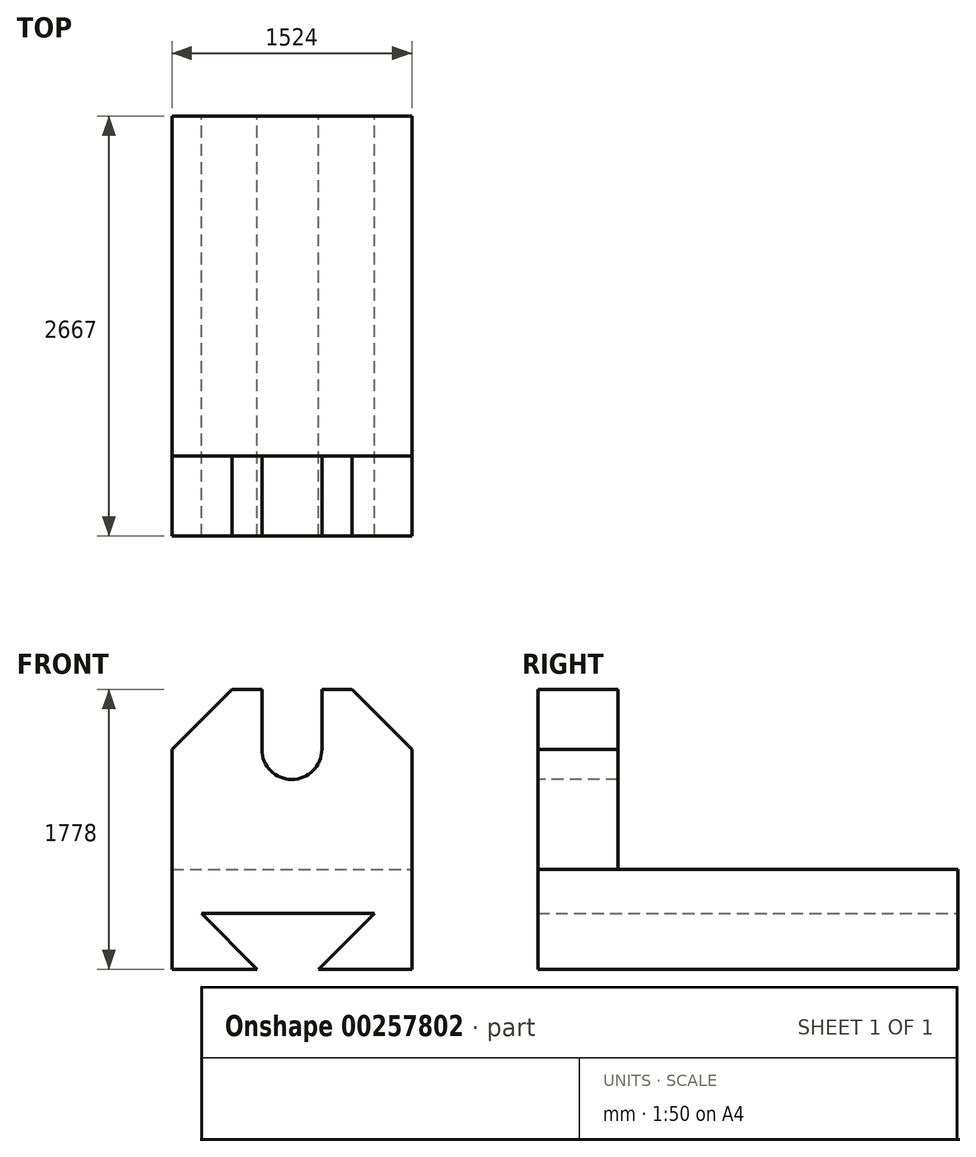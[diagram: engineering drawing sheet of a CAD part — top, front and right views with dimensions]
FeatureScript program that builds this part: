
annotation { "Feature Type Name" : "Feature", "Feature Type Description" : "" }
export const myFeature = defineFeature(function(context is Context, id is Id, definition is map)
    precondition{}
    {
        {
            var Q0;
            Q0=qCreatedBy(makeId("Top.planeOp"),FACE);
            var sketch = newSketch(context, id + "F0", { "sketchPlane" : qUnion([Q0])});
            skLineSegment(sketch, "E0.bottom", {"start": v(-839.6, 1330.28) * mm, "end": v(684.4, 1330.28) * mm});
            skLineSegment(sketch, "E0.top", {"start": v(-839.6, -1336.72) * mm, "end": v(684.4, -1336.72) * mm});
            skLineSegment(sketch, "E0.left", {"start": v(-839.6, 1330.28) * mm, "end": v(-839.6, -1336.72) * mm});
            skLineSegment(sketch, "E0.right", {"start": v(684.4, 1330.28) * mm, "end": v(684.4, -1336.72) * mm});
            skSolve(sketch);
        }
        {
            var Q0;
            Q0 = qSketchRegion(id + "F0", true);
            extrude(context, id + "F1", {"entities" : qUnion([Q0]), "oppositeDirection" : true, "depth" : 635 * mm});
        }
        {
            var Q0;
            Q0=makeQuery(id+"F1.opExtrude","SWEPT_FACE",FACE,{"disambiguationData":[OSD([sQuery(id+"F0.wireOp",EDGE,"E0.top")])]});
            var sketch = newSketch(context, id + "F2", { "sketchPlane" : qUnion([Q0])});
            skSolve(sketch);
        }
        {
            var Q0;
            {var subQ0=sQuery(id+"F0.wireOp",EDGE,"E0.top");Q0=makeQuery(id+"F2.imprint","IMPRINT",FACE,{"disambiguationData":[TD([[makeQuery(id+"F2.imprint","IMPRINT",EDGE,{"derivedFrom":makeQuery(id+"F1.opExtrude","CAP_EDGE",EDGE,{"disambiguationData":[OSD([subQ0])],"isStart":true})}),-1.0]])]});}
            var sketch = newSketch(context, id + "F3", { "sketchPlane" : qUnion([Q0])});
            skLineSegment(sketch, "E1", {"start": v(-1531.1, 762) * mm, "end": v(1578.52, 762) * mm, "construction": true});
            skPoint(sketch, "E2", {"position": v(-839.6, 0) * mm});
            skPoint(sketch, "E3", {"position": v(684.37, 0) * mm});
            skLineSegment(sketch, "E4", {"start": v(-839.6, 0) * mm, "end": v(-839.6, 762) * mm});
            skLineSegment(sketch, "E5", {"start": v(684.37, 0) * mm, "end": v(684.37, 762) * mm});
            skLineSegment(sketch, "E6", {"start": v(-77.6, 937.44) * mm, "end": v(-77.6, -1034.68) * mm, "construction": true});
            skArc(sketch, "E7", {"start": v(-268.1, 762) * mm, "mid": v(-77.6, 571.5) * mm, "end": v(112.9, 762) * mm});
            skLineSegment(sketch, "E8", {"start": v(-268.1, 762) * mm, "end": v(-268.1, 1143) * mm});
            skLineSegment(sketch, "E9", {"start": v(112.9, 762) * mm, "end": v(112.9, 1143) * mm});
            skLineSegment(sketch, "E10", {"start": v(-268.1, 1143) * mm, "end": v(-458.6, 1143) * mm});
            skLineSegment(sketch, "E11", {"start": v(112.9, 1143) * mm, "end": v(303.37, 1143) * mm});
            skLineSegment(sketch, "E12", {"start": v(-458.6, 1143) * mm, "end": v(-839.6, 762) * mm});
            skLineSegment(sketch, "E13", {"start": v(303.37, 1143) * mm, "end": v(684.37, 762) * mm});
            skSolve(sketch);
        }
        {
            var Q0;
            Q0 = qSketchRegion(id + "F3", true);
            var Q1;
            {var subQ0=sQuery(id+"F3.wireOp",EDGE,"E4");Q1=makeQuery(id+"F3.imprint","IMPRINT",FACE,{"disambiguationData":[TD([[makeQuery(id+"F3.imprint","IMPRINT",EDGE,{"derivedFrom":subQ0}),-1.0]])]});}
            extrude(context, id + "F4", {"entities" : qUnion([Q0, Q1]), "operationType" : NewBodyOperationType.ADD, "oppositeDirection" : true, "depth" : 508 * mm});
        }
        {
            var Q0;
            Q0=makeQuery(id+"F1.opExtrude","SWEPT_FACE",FACE,{"disambiguationData":[OSD([sQuery(id+"F0.wireOp",EDGE,"E0.bottom")])]});
            var sketch = newSketch(context, id + "F5", { "sketchPlane" : qUnion([Q0])});
            skLineSegment(sketch, "E14", {"start": v(-92.32, -635) * mm, "end": v(-447.92, -279.4) * mm});
            skLineSegment(sketch, "E15", {"start": v(297.14, -635) * mm, "end": v(652.74, -279.4) * mm});
            skLineSegment(sketch, "E16", {"start": v(-447.92, -279.4) * mm, "end": v(662.06, -279.4) * mm});
            skLineSegment(sketch, "E17", {"start": v(-92.32, -635) * mm, "end": v(-92.32, -854.68) * mm});
            skLineSegment(sketch, "E18", {"start": v(-92.32, -854.68) * mm, "end": v(309.4, -854.68) * mm});
            skLineSegment(sketch, "E19", {"start": v(309.4, -854.68) * mm, "end": v(297.14, -635) * mm});
            skSolve(sketch);
        }
        {
            var Q0;
            Q0 = qSketchRegion(id + "F5", true);
            extrude(context, id + "F6", {"entities" : qUnion([Q0]), "operationType" : NewBodyOperationType.REMOVE, "oppositeDirection" : true, "depth" : 2667 * mm});
        }
    });
